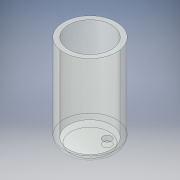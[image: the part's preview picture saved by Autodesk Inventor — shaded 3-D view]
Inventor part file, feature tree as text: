
AUTODESK INVENTOR PART (.ipt)
format: ipt  version: 2018 (Build 220112000, 112)  size: 124,416 bytes
history: native  units: in
note: dims shown in document units (in); Inventor stores cm internally (conversion verified against a paired STEP export)
features: extrude x2, sketch x2, shell x1, fillet x1
ambient origin geometry x8: Origin, YZ Plane, XZ Plane, XY Plane, X Axis, Y Axis, Z Axis, Center Point
bodies: Solid1 (feature_tree)
feature tree (6):
  extrude  "Extrusion1"  Depth=0.8in TaperAngle=0.0deg
  shell  "Shell1"  Thickness=0.043in
  fillet  "Fillet1"  Radius=0.0625in
  extrude  "Extrusion2"  Depth=0.8in TaperAngle=0.0deg
  sketch  "Sketch1"  dims[d0=0.46in d1=0.8in d2=0.0in d3=0.043in d4=0.0625in]
  sketch  "Sketch2"  dims[d5=0.075in d6=0.8in d7=0.0in]
